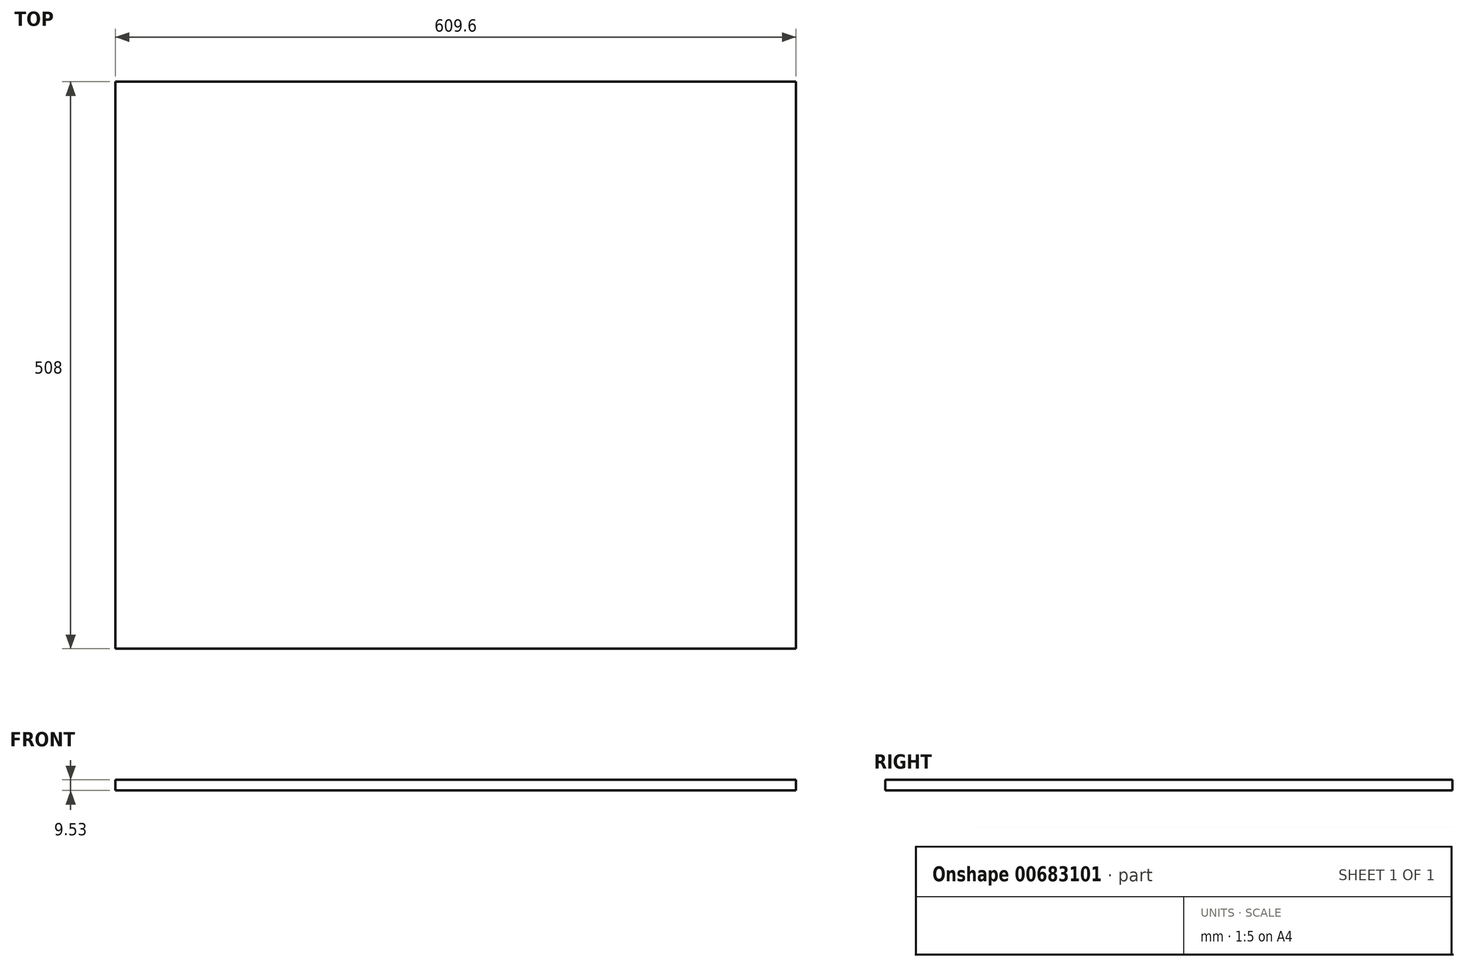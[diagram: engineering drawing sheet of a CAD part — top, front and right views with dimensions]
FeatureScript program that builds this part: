
annotation { "Feature Type Name" : "Feature", "Feature Type Description" : "" }
export const myFeature = defineFeature(function(context is Context, id is Id, definition is map)
    precondition{}
    {
        {
            var Q0;
            Q0=qCreatedBy(makeId("Top.planeOp"),FACE);
            var sketch = newSketch(context, id + "F0", { "sketchPlane" : qUnion([Q0])});
            skLineSegment(sketch, "E0.bottom", {"start": v(304.8, 254) * mm, "end": v(-304.8, 254) * mm});
            skLineSegment(sketch, "E0.top", {"start": v(304.8, -254) * mm, "end": v(-304.8, -254) * mm});
            skLineSegment(sketch, "E0.left", {"start": v(304.8, 254) * mm, "end": v(304.8, -254) * mm});
            skLineSegment(sketch, "E0.right", {"start": v(-304.8, 254) * mm, "end": v(-304.8, -254) * mm});
            skPoint(sketch, "E0.middle", {"position": v(0, 0) * mm});
            skSolve(sketch);
        }
        {
            var Q0;
            Q0 = qSketchRegion(id + "F0", true);
            extrude(context, id + "F1", {"entities" : qUnion([Q0]), "depth" : 9.52 * mm, "offsetDistance" : 25.4 * mm});
        }
    });
